# Revit family: Plumbing-Fix_Faucet-Touchless_Stern_Extreme-Mixer-1000-Plus
name_source: partatom
category: Plumbing Fixtures
units: mm (PartAtom-declared; Revit-internal decimal feet)

## family parameters
Classification Number = 23.45.55.17
Cut with Voids When Loaded = No
Enable Cutting in Views = No
Host = Face
Maintain Annotation Orientation = No
Part Type = Normal
Room Calculation Point = No
Round Connector Dimension = Use Diameter
Shared = No

## types (1)
- Default
    Assembly Code = D2010300
    Available Options = as Specified
    CW Connection = Yes
    CWFU = 1
    Cost = 0 $
    Default Elevation = 0' - 0"
    Description = Stern Touchless Deck Mounted Mixing Faucet - Extreme 1000 Plus B as Specified
    Expected Lifespan (Years) = 0
    Extension Option Selection = 1
    HW Connection = Yes
    HWFU = 1
    Keynote = 22 40 00
    Link to Type Catalog = https://www.arcat.com
    Maintenance Schedule (Months) = 0
    Manufacturer = Stern Engineering
    Manufacturer Website = http://www.sternfaucets.com
    Model = Extreme 1000 Plus B
    Operating Pressure Range = 7.26 - 116 PSI  ;  0.5 - 8 bar
    Operating Temperature Range = Up to 149 F / 65 C
    Piping_Flow = 0 GPM
    Piping_Inlet Diameter = 0"
    Power Supply = 9V Battery
    Product Data = http://www.arcat.com
    Product Features = Security Shut Off Timer
    Revision = R1_2018-04
    Sales Information = http://www.sternfaucets.com
    Spout Reach = 0' - 0"
    Standards Conformance = as Specified
    Type Comments = as Specified
    URL = http://www.sternfaucets.com
    Unit Width = 0' - 2"
    Vent Connection = No
    WFU = 0
    Warranty Duration (Years) = 2
    Waste Connection = No

## geometry (parser evidence)
native form markers: Sweep x2
no freeform markers — native parametric forms only
